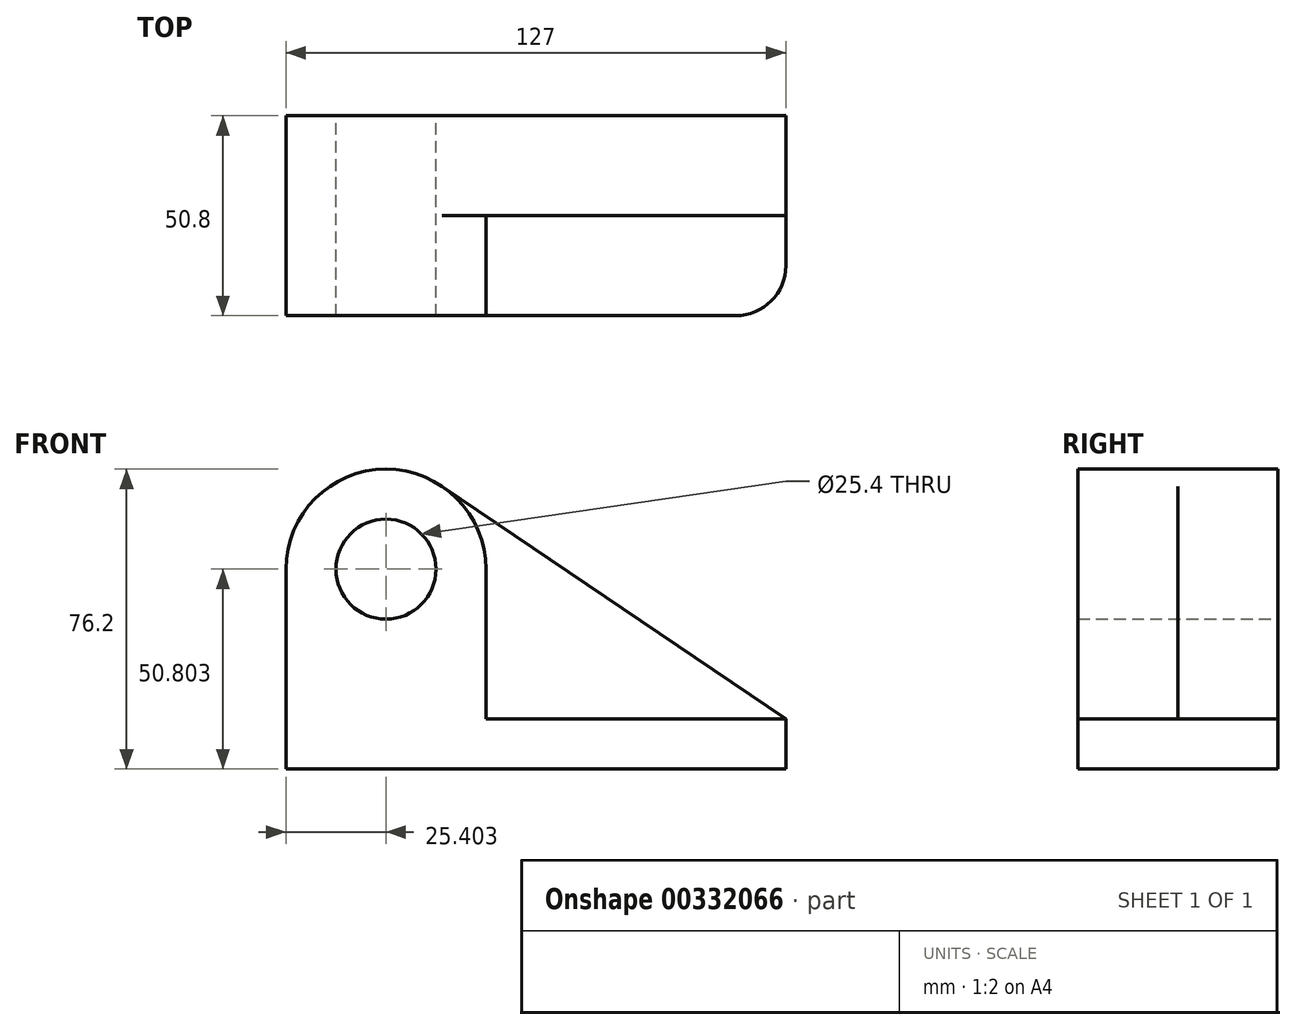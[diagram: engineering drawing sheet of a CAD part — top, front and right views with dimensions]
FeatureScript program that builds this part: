
annotation { "Feature Type Name" : "Feature", "Feature Type Description" : "" }
export const myFeature = defineFeature(function(context is Context, id is Id, definition is map)
    precondition{}
    {
        {
            var Q0;
            Q0=qCreatedBy(makeId("Front.planeOp"),FACE);
            var sketch = newSketch(context, id + "F0", { "sketchPlane" : qUnion([Q0])});
            skCircle(sketch, "E0", {"center": v(-41.08, -4.68) * mm, "radius": 12.7 * mm});
            skArc(sketch, "E1", {"start": v(-26.84, 16.36) * mm, "mid": v(-52.98, 17.76) * mm, "end": v(-66.48, -4.68) * mm});
            skLineSegment(sketch, "E2", {"start": v(-66.48, -4.68) * mm, "end": v(-66.48, -55.48) * mm});
            skLineSegment(sketch, "E3", {"start": v(-66.48, -55.48) * mm, "end": v(60.52, -55.48) * mm});
            skLineSegment(sketch, "E4", {"start": v(60.52, -55.48) * mm, "end": v(60.52, -42.78) * mm});
            skLineSegment(sketch, "E5", {"start": v(60.52, -42.78) * mm, "end": v(-26.84, 16.36) * mm});
            skSolve(sketch);
        }
        {
            var Q0;
            Q0=makeQuery(id+"F0.imprint","IMPRINT",FACE,{"disambiguationData":[TD([[makeQuery(id+"F0.imprint","IMPRINT",EDGE,{"derivedFrom":sQuery(id+"F0.wireOp",EDGE,"E0")}),-1.0]])]});
            extrude(context, id + "F1", {"entities" : qUnion([Q0]), "depth" : 25.4 * mm});
        }
        {
            var Q0;
            Q0=makeQuery(id+"F1.opExtrude","CAP_FACE",FACE,{"disambiguationData":[OSD([sQuery(id+"F0.wireOp",EDGE,"E0"),sQuery(id+"F0.wireOp",EDGE,"E1"),sQuery(id+"F0.wireOp",EDGE,"E2"),sQuery(id+"F0.wireOp",EDGE,"E3"),sQuery(id+"F0.wireOp",EDGE,"E4"),sQuery(id+"F0.wireOp",EDGE,"E5")])],"isStart":false});
            var sketch = newSketch(context, id + "F2", { "sketchPlane" : qUnion([Q0])});
            skCircle(sketch, "E6", {"center": v(-41.08, -4.68) * mm, "radius": 12.7 * mm});
            skCircle(sketch, "E7", {"center": v(-41.08, -4.68) * mm, "radius": 25.4 * mm});
            skLineSegment(sketch, "E8.bottom", {"start": v(60.52, -42.78) * mm, "end": v(-15.68, -42.78) * mm});
            skLineSegment(sketch, "E8.top", {"start": v(60.52, -55.48) * mm, "end": v(-66.48, -55.48) * mm});
            skLineSegment(sketch, "E8.left", {"start": v(60.52, -42.78) * mm, "end": v(60.52, -55.48) * mm});
            skLineSegment(sketch, "E8.right", {"start": v(-66.48, -42.78) * mm, "end": v(-66.48, -55.48) * mm});
            skLineSegment(sketch, "E9", {"start": v(-15.68, -4.68) * mm, "end": v(-15.68, -42.78) * mm});
            skLineSegment(sketch, "E10", {"start": v(-66.48, -4.68) * mm, "end": v(-15.68, -4.68) * mm});
            skSolve(sketch);
        }
        {
            var Q0;
            Q0 = qSketchRegion(id + "F2", true);
            extrude(context, id + "F3", {"entities" : qUnion([Q0]), "operationType" : NewBodyOperationType.ADD, "depth" : 25.4 * mm});
        }
        {
            var Q0;
            {var subQ2=sQuery(id+"F2.wireOp",EDGE,"E10");var subQ5=sQuery(id+"F2.wireOp",EDGE,"E6");var subQ6=makeQuery(id+"F2.imprint","INTERSECT",VERTEX,{"disambiguationData":[OD(0.0)],"derivedFrom":[subQ5,subQ2]});Q0=makeQuery(id+"F2.imprint","IMPRINT",FACE,{"disambiguationData":[TD([[makeQuery(id+"F2.imprint","IMPRINT",EDGE,{"disambiguationData":[TD([[subQ6,1.0]])],"derivedFrom":subQ5}),-1.0]])]});}
            var Q1;
            {var subQ0=sQuery(id+"F2.wireOp",EDGE,"E10");var subQ1=sQuery(id+"F2.wireOp",EDGE,"E6");var subQ2=makeQuery(id+"F2.imprint","INTERSECT",VERTEX,{"disambiguationData":[OD(0.0)],"derivedFrom":[subQ1,subQ0]});Q1=makeQuery(id+"F2.imprint","IMPRINT",FACE,{"disambiguationData":[TD([[makeQuery(id+"F2.imprint","IMPRINT",EDGE,{"disambiguationData":[TD([[subQ2,-1.0]])],"derivedFrom":subQ1}),-1.0]])]});}
            var Q2;
            Q2=makeQuery(id+"F2.imprint","IMPRINT",FACE,{"disambiguationData":[TD([[makeQuery(id+"F2.imprint","IMPRINT",EDGE,{"derivedFrom":sQuery(id+"F2.wireOp",EDGE,"E8.bottom")}),1.0]])]});
            extrude(context, id + "F4", {"entities" : qUnion([Q0, Q1, Q2]), "operationType" : NewBodyOperationType.ADD, "depth" : 25.4 * mm});
        }
        {
            var Q0;
            Q0=makeQuery(id+"F4.opExtrude","CAP_EDGE",EDGE,{"disambiguationData":[OSD([sQuery(id+"F2.wireOp",EDGE,"E8.left")])],"isStart":false});
            fillet(context, id + "F5", {"entities" : qUnion([Q0]), "radius" : 12.7 * mm, "tangentPropagation" : true, "allowEdgeOverflow" : false});
        }
    });
